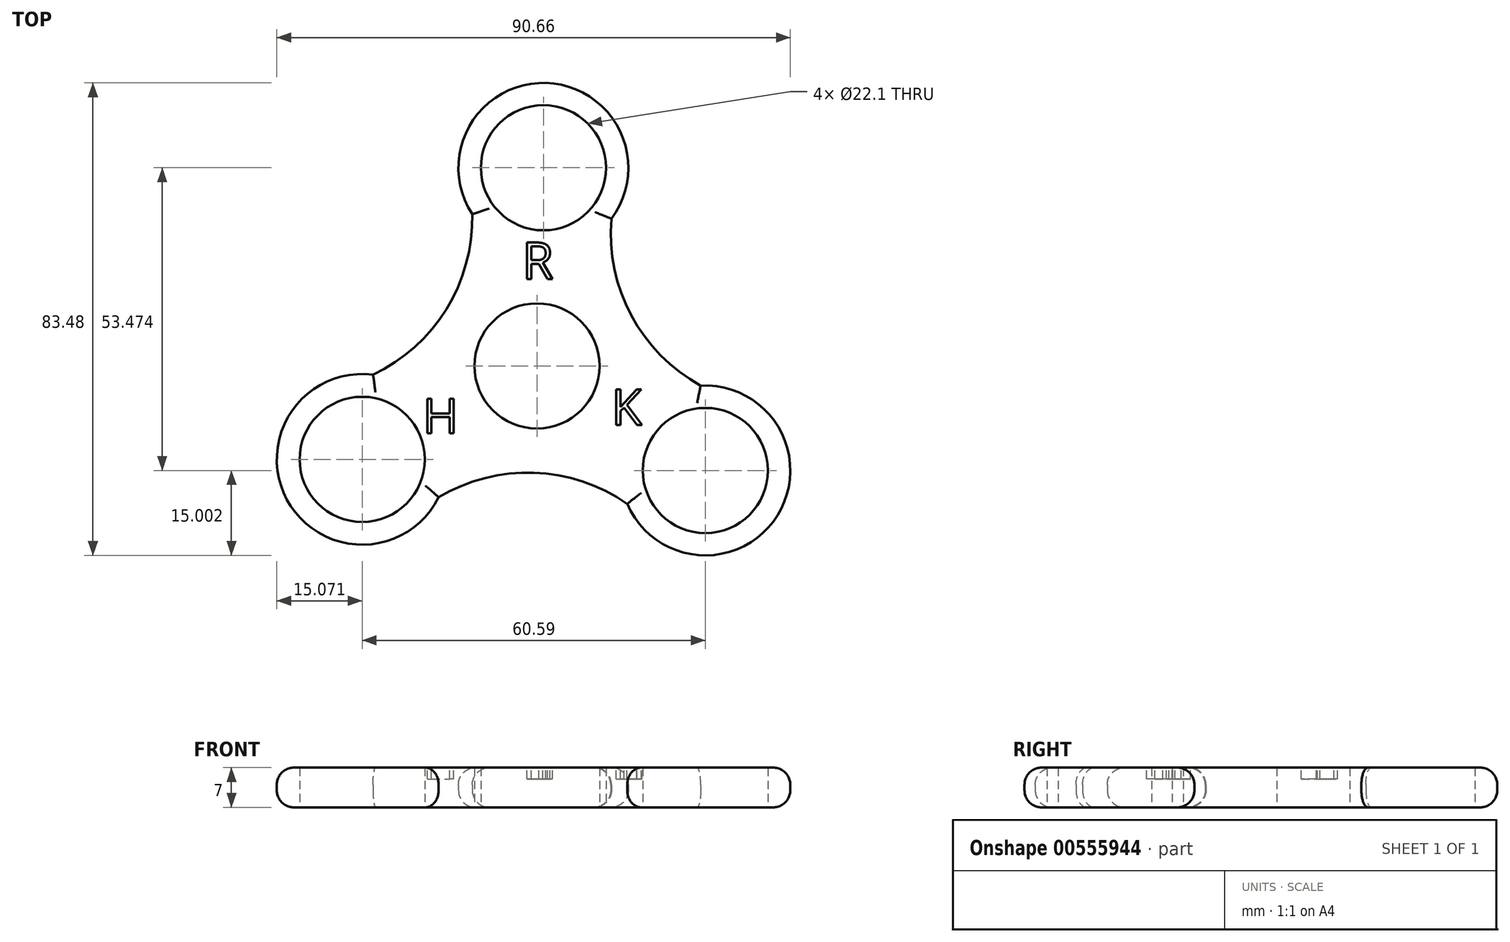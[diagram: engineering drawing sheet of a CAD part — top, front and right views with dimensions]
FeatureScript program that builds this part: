
annotation { "Feature Type Name" : "Feature", "Feature Type Description" : "" }
export const myFeature = defineFeature(function(context is Context, id is Id, definition is map)
    precondition{}
    {
        {
            var Q0;
            Q0=qCreatedBy(makeId("Top.planeOp"),FACE);
            var sketch = newSketch(context, id + "F0", { "sketchPlane" : qUnion([Q0])});
            skCircle(sketch, "E0", {"center": v(-1.14, 16.5) * mm, "radius": 11.05 * mm});
            skCircle(sketch, "E1", {"center": v(0, 51.5) * mm, "radius": 11.05 * mm});
            skCircle(sketch, "E2", {"center": v(-32, 0) * mm, "radius": 11.05 * mm});
            skCircle(sketch, "E3", {"center": v(28.6, -1.97) * mm, "radius": 11.05 * mm});
            skCircle(sketch, "E4", {"center": v(-1.14, 16.5) * mm, "radius": 15 * mm});
            skCircle(sketch, "E5", {"center": v(0, 51.5) * mm, "radius": 15 * mm});
            skCircle(sketch, "E6", {"center": v(-32, 0) * mm, "radius": 15.07 * mm});
            skCircle(sketch, "E7", {"center": v(28.6, -1.97) * mm, "radius": 15 * mm});
            skArc(sketch, "E8.MirrorCS", {"start": v(-25.4, -12.35) * mm, "mid": v(-1.75, -2.37) * mm, "end": v(21.2, -13.86) * mm});
            skLineSegment(sketch, "E9", {"start": v(-32, 0) * mm, "end": v(-1.14, 16.5) * mm});
            skLineSegment(sketch, "E10", {"start": v(-32, 0) * mm, "end": v(-25.4, -12.35) * mm});
            skLineSegment(sketch, "E11", {"start": v(-1.14, 16.5) * mm, "end": v(28.6, -1.97) * mm});
            skLineSegment(sketch, "E12", {"start": v(28.6, -1.97) * mm, "end": v(21.2, -13.86) * mm});
            skArc(sketch, "E13.MirrorCS", {"start": v(-38.6, 12.35) * mm, "mid": v(-17.18, 26.48) * mm, "end": v(-14, 51.94) * mm});
            skLineSegment(sketch, "E14.MirrorCS", {"start": v(-1.14, 16.5) * mm, "end": v(0, 51.49) * mm});
            skLineSegment(sketch, "E15.MirrorCS", {"start": v(0, 51.49) * mm, "end": v(-14, 51.94) * mm});
            skLineSegment(sketch, "E16.MirrorCS", {"start": v(-32, 0) * mm, "end": v(-38.6, 12.35) * mm});
            skArc(sketch, "E17.MirrorCS", {"start": v(14, 51.03) * mm, "mid": v(15.52, 25.42) * mm, "end": v(35.98, 9.92) * mm});
            skLineSegment(sketch, "E18.MirrorCS", {"start": v(28.6, -1.97) * mm, "end": v(35.98, 9.92) * mm});
            skSolve(sketch);
        }
        {
            var Q0;
            Q0=qSketchRegion(id+"F0",true);
            var Q1;
            {var subQ0=sQuery(id+"F0.wireOp",EDGE,"E9");var subQ1=sQuery(id+"F0.wireOp",EDGE,"E0");var subQ2=makeQuery(id+"F0.imprint","INTERSECT",VERTEX,{"derivedFrom":[subQ1,subQ0]});Q1=makeQuery(id+"F0.imprint","IMPRINT",FACE,{"disambiguationData":[TD([[makeQuery(id+"F0.imprint","IMPRINT",EDGE,{"disambiguationData":[TD([[subQ2,1.0]])],"derivedFrom":subQ1}),-1.0]])]});}
            var Q2;
            {var subQ0=sQuery(id+"F0.wireOp",EDGE,"E9");var subQ1=sQuery(id+"F0.wireOp",EDGE,"E0");var subQ2=makeQuery(id+"F0.imprint","INTERSECT",VERTEX,{"derivedFrom":[subQ1,subQ0]});Q2=makeQuery(id+"F0.imprint","IMPRINT",FACE,{"disambiguationData":[TD([[makeQuery(id+"F0.imprint","IMPRINT",EDGE,{"disambiguationData":[TD([[subQ2,-1.0]])],"derivedFrom":subQ1}),-1.0]])]});}
            var Q3;
            {var subQ0=sQuery(id+"F0.wireOp",EDGE,"E14.MirrorCS");var subQ1=sQuery(id+"F0.wireOp",EDGE,"E0");var subQ2=makeQuery(id+"F0.imprint","INTERSECT",VERTEX,{"derivedFrom":[subQ1,subQ0]});Q3=makeQuery(id+"F0.imprint","IMPRINT",FACE,{"disambiguationData":[TD([[makeQuery(id+"F0.imprint","IMPRINT",EDGE,{"disambiguationData":[TD([[subQ2,1.0]])],"derivedFrom":subQ1}),-1.0]])]});}
            extrude(context, id + "F1", {"entities" : qUnion([Q0, Q1, Q2, Q3]), "depth" : 7 * mm});
        }
        {
            var Q0;
            Q0=makeQuery(id+"F1.opExtrude","CAP_EDGE",EDGE,{"disambiguationData":[OSD([sQuery(id+"F0.wireOp",EDGE,"E5")])],"isStart":true});
            var Q1;
            Q1=makeQuery(id+"F1.opExtrude","CAP_EDGE",EDGE,{"disambiguationData":[OSD([sQuery(id+"F0.wireOp",EDGE,"E13.MirrorCS")])],"isStart":true});
            var Q2;
            Q2=makeQuery(id+"F1.opExtrude","CAP_EDGE",EDGE,{"disambiguationData":[OSD([sQuery(id+"F0.wireOp",EDGE,"E6")])],"isStart":true});
            var Q3;
            Q3=makeQuery(id+"F1.opExtrude","CAP_EDGE",EDGE,{"disambiguationData":[OSD([sQuery(id+"F0.wireOp",EDGE,"E8.MirrorCS")])],"isStart":true});
            var Q4;
            Q4=makeQuery(id+"F1.opExtrude","CAP_EDGE",EDGE,{"disambiguationData":[OSD([sQuery(id+"F0.wireOp",EDGE,"E7")])],"isStart":true});
            var Q5;
            Q5=makeQuery(id+"F1.opExtrude","CAP_EDGE",EDGE,{"disambiguationData":[OSD([sQuery(id+"F0.wireOp",EDGE,"E17.MirrorCS")])],"isStart":true});
            fillet(context, id + "F2", {"entities" : qUnion([Q0, Q1, Q2, Q3, Q4, Q5]), "radius" : 3 * mm, "tangentPropagation" : true, "allowEdgeOverflow" : false});
        }
        {
            var Q0;
            Q0=makeQuery(id+"F1.opExtrude","CAP_EDGE",EDGE,{"disambiguationData":[OSD([sQuery(id+"F0.wireOp",EDGE,"E6")])],"isStart":false});
            var Q1;
            Q1=makeQuery(id+"F1.opExtrude","CAP_EDGE",EDGE,{"disambiguationData":[OSD([sQuery(id+"F0.wireOp",EDGE,"E13.MirrorCS")])],"isStart":false});
            var Q2;
            Q2=makeQuery(id+"F1.opExtrude","CAP_EDGE",EDGE,{"disambiguationData":[OSD([sQuery(id+"F0.wireOp",EDGE,"E5")])],"isStart":false});
            var Q3;
            Q3=makeQuery(id+"F1.opExtrude","CAP_EDGE",EDGE,{"disambiguationData":[OSD([sQuery(id+"F0.wireOp",EDGE,"E17.MirrorCS")])],"isStart":false});
            var Q4;
            Q4=makeQuery(id+"F1.opExtrude","CAP_EDGE",EDGE,{"disambiguationData":[OSD([sQuery(id+"F0.wireOp",EDGE,"E7")])],"isStart":false});
            var Q5;
            Q5=makeQuery(id+"F1.opExtrude","CAP_EDGE",EDGE,{"disambiguationData":[OSD([sQuery(id+"F0.wireOp",EDGE,"E8.MirrorCS")])],"isStart":false});
            fillet(context, id + "F3", {"entities" : qUnion([Q0, Q1, Q2, Q3, Q4, Q5]), "radius" : 3 * mm, "tangentPropagation" : true, "allowEdgeOverflow" : false});
        }
        {
            var Q0;
            Q0=makeQuery(id+"F1.opExtrude","CAP_FACE",FACE,{"disambiguationData":[OSD([sQuery(id+"F0.wireOp",EDGE,"E0"),sQuery(id+"F0.wireOp",EDGE,"E1"),sQuery(id+"F0.wireOp",EDGE,"E2"),sQuery(id+"F0.wireOp",EDGE,"E3"),sQuery(id+"F0.wireOp",EDGE,"E5"),sQuery(id+"F0.wireOp",EDGE,"E6"),sQuery(id+"F0.wireOp",EDGE,"E7"),sQuery(id+"F0.wireOp",EDGE,"E8.MirrorCS"),sQuery(id+"F0.wireOp",EDGE,"E13.MirrorCS"),sQuery(id+"F0.wireOp",EDGE,"E17.MirrorCS")])],"isStart":false});
            var sketch = newSketch(context, id + "F4", { "sketchPlane" : qUnion([Q0])});
            skText(sketch, "E19", { "text": "R", "fontName": "OpenSans-Regular.ttf"});
            skText(sketch, "E20", { "text": "H", "fontName": "OpenSans-Regular.ttf"});
            skText(sketch, "E21", { "text": "K", "fontName": "OpenSans-Regular.ttf"});
            const initialGuessF4  = {"E19": [-0.0038, 0.03187, 1, 0, 0.00649], "E20": [-0.0213, 0.0046, 1, 0, 0.00613], "E21": [0.01199, 0.00604, 1, 0, 0.00637]};
            skSetInitialGuess(sketch, initialGuessF4);
            skSolve(sketch);
        }
        {
            var Q0;
            Q0=qSketchRegion(id+"F4",true);
            extrude(context, id + "F5", {"entities" : qUnion([Q0]), "operationType" : NewBodyOperationType.REMOVE, "oppositeDirection" : true, "depth" : 2 * mm});
        }
    });
